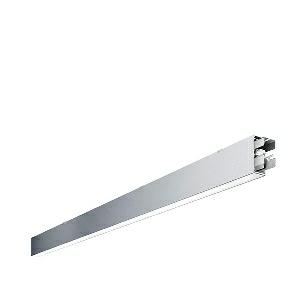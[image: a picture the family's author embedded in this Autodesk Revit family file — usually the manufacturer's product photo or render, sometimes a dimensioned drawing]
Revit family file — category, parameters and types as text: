
# Revit family: dotoo_line_-_dla_3000_830_d_mid_00807971_501a
name_source: partatom
category: Lighting Fixtures
units: mm (PartAtom-declared; Revit-internal decimal feet)

## family parameters
Cut with Voids When Loaded = No
Host = Face
Light Source = No
Part Type = Normal
Room Calculation Point = No
Round Connector Dimension = Use Diameter
Shared = No

## types (1)
- DOTOO.line - DLA 3000/830/D MID (1 x LED, 2650 lm, 3000K)
    Apparent Load = 26 VA
    Approval mark = CE
    CIE Flux Codes = 67 91 98 100 100
    Color Rendering = 80-89
    Color Temperature = 3000K
    Control Gear = Electronic ballast
    Default Elevation = 1800 mm
    Description = DLA 3000/830/D|Surface-mounted luminaire.|light source: LED|work equipment: Adjustable electronic ballast, digital DALI|connected load: 220-240 V, 50/60 Hz|Power consumption: approx. 26 W|luminous flux: 2650 lm|luminous efficacy: 101 lm/W|light distribution: Direct|colour temperature: Warm white, ca. 3000 K|class of protection: I|technology: Continuously dimmable|mains lead: Connector|glare control: Prism aperture|special features: DALI Load 1x, TouchDIM - dimming via standard switch, Through-wired, up to 18 m on one mains connection, Flicker-free, Suitable as emergency lighting, Mechanical and electrical connection of the individual modules without tools|
    Frequency = 50 Hz
    Height = 110 mm
    Lamp = 1 x LED
    Lamp Light Flux = 2650 lm
    Lamp count = 1
    Length = 2244 mm
    Luminous efficacy = 102 lm/W
    Manufacturer = Waldmann
    ModVariant = No
    Model = 00807971
    Mounting Place = Ceiling
    Mounting Type = Surface mounted
    Number of Poles = 1
    OnlyDefault = Yes
    Power Factor = 1
    Product Name = DOTOO.line - DLA 3000/830/D MID
    Product group = Ceiling mounted luminaire
    ProductGroupID = 3
    Protection Class = Protection class I
    Protection Degree = IP 40
    RLX_Detail_Level = 1
    RLX_Emergency_Light_Flux = 0 lm
    RLX_Emergency_Type = 0
    RLX_Emergency_Type_DB = No
    RlxData = <blob elided: 22629 chars, md5=d0d81bca>
    Socket = socket
    Standby Power = 0 W
    System Light Flux = 2650 lm
    System Power = 26 W
    Type Comments = Product without accessories
    Type Image = 114382000-00807959.jpg
    URL = http://relux.com
    VarID = ---
    Voltage = 230 V
    Voltage Range = 220-240 V
    Weight = 0.00 kg
    Width = 60 mm  [stored 0.19685 ft]

note: [stored X ft] marks values corroborated as IEEE doubles in the binary element streams (Revit-internal decimal feet)

## geometry (parser evidence)
native form markers: Blend x4, Sweep x12
no freeform markers — native parametric forms only
